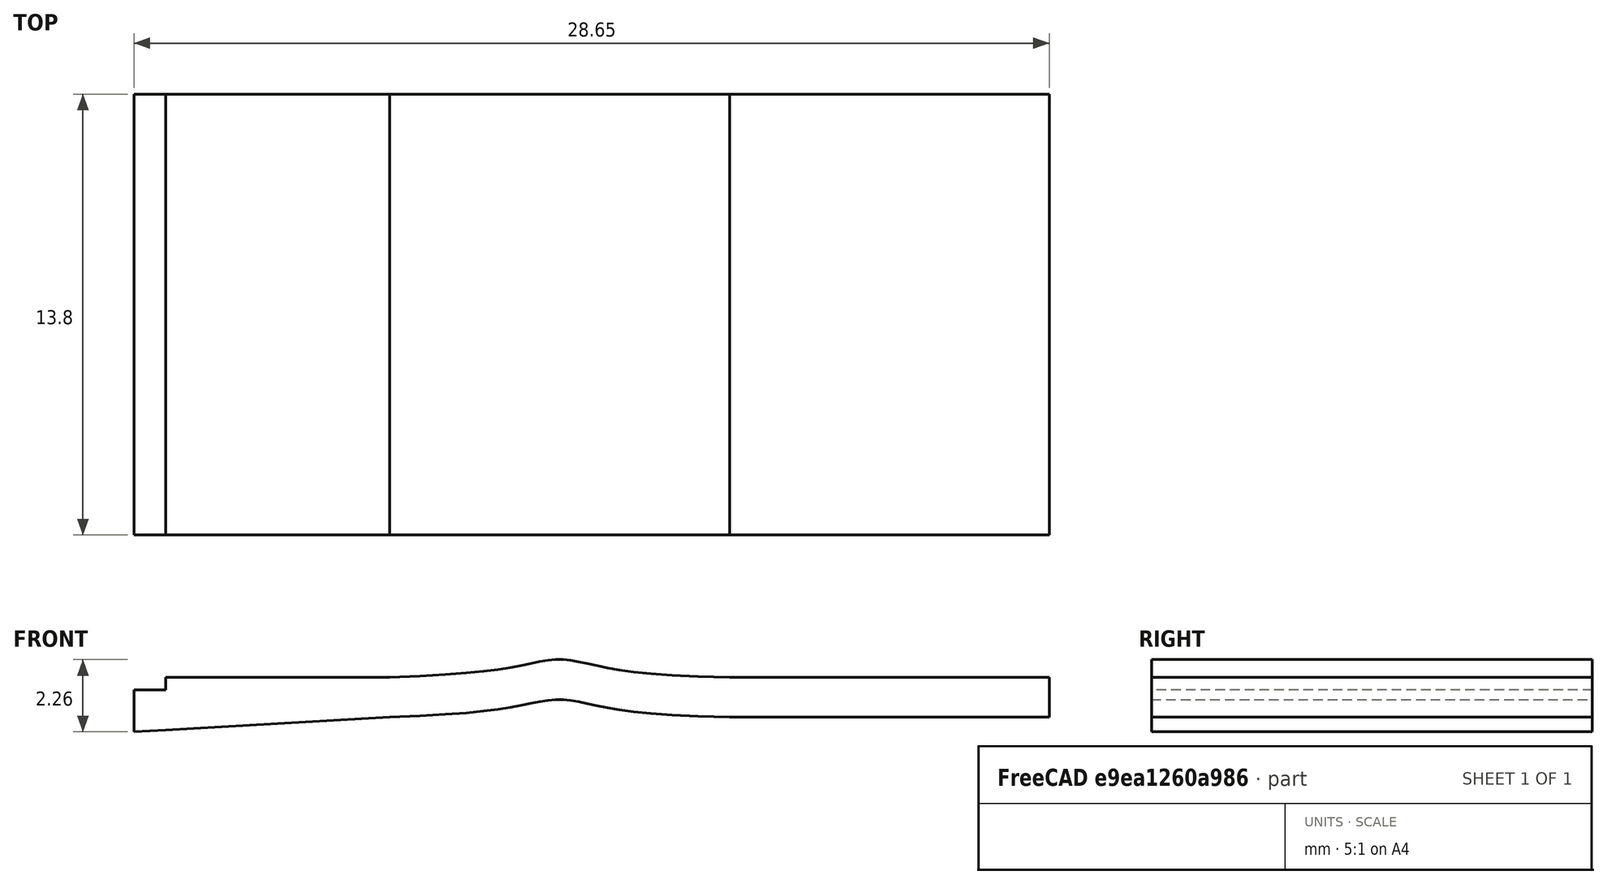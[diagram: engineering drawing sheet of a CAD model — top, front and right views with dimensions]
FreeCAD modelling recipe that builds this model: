
FCSTD DOCUMENT  (FreeCAD 0.21R33668 +26 (Git))
Label: HMV080_flex-slot-complete_channel
License: All rights reserved
LicenseURL: http://en.wikipedia.org/wiki/All_rights_reserved
objects: Sketcher::SketchObject×1, PartDesign::Pad×1, PartDesign::Body×1
note: 4 computed .brp shape members not serialized (recipe doc carries the construction recipe); baked Part::Feature solids carry a one-line shape summary decoded from their .brp

FEATURE [Sketcher::SketchObject] Sketch
  FullyConstrained = true
  MapMode = 5
  Placement = pos=(0,0,0) rot=(1,0,0;1.5708rad)
  Support = -> [XZ_Plane]
  sketch-geometry (37):
    g0: GeomPoint X=18.65 Y=0 Z=0
    g1: GeomPoint X=13.32 Y=0.7 Z=0
    g2: LineSegment StartX=18.65 StartY=0 StartZ=0 EndX=28.65 EndY=0 EndZ=0
    g3: LineSegment StartX=28.65 StartY=-1.25 StartZ=0 EndX=28.65 EndY=0 EndZ=0
    g4-g10: Circle x7 (B-spline internal-alignment scaffolding for g11; pole/knot coordinates omitted)
    g11: BSplineCurve PolesCount=7 KnotsCount=5 Degree=3 IsPeriodic=0
    g12-g16: GeomPoint x5 (B-spline internal-alignment scaffolding for g11; pole/knot coordinates omitted)
    g17: LineSegment StartX=28.65 StartY=-1.25 StartZ=0 EndX=18.65 EndY=-1.25 EndZ=0
    g18-g24: Circle x7 (B-spline internal-alignment scaffolding for g25; pole/knot coordinates omitted)
    g25: BSplineCurve PolesCount=7 KnotsCount=5 Degree=3 IsPeriodic=0
    g26-g30: GeomPoint x5 (B-spline internal-alignment scaffolding for g25; pole/knot coordinates omitted)
    g31: LineSegment StartX=1 StartY=-0.4 StartZ=0 EndX=1 EndY=0 EndZ=0
    g32: LineSegment StartX=1 StartY=0 StartZ=0 EndX=8 EndY=0 EndZ=0
    g33: LineSegment StartX=8 StartY=-1.25 StartZ=0 EndX=1 EndY=-1.65 EndZ=0
    g34: LineSegment StartX=1 StartY=-1.65 StartZ=0 EndX=0 EndY=-1.70714 EndZ=0
    g35: LineSegment StartX=0 StartY=-1.70714 StartZ=0 EndX=0 EndY=-0.4 EndZ=0
    g36: LineSegment StartX=1 StartY=-0.4 StartZ=0 EndX=0 EndY=-0.4 EndZ=0
  constraints (69):
    c: PointOnObject(g2,g-1)
    c: DistanceX(g-1,g2) = 28.65
    c: Coincident(g2,g0)
    c: Coincident(g3,g2)
    c: Vertical(g3)
    c: DistanceY(g3,g3) = 1.25
    c: Horizontal(g2)
    c: DistanceY(g-1,g1) = 0.7
    c: Weight(g4) = 1
    c: Coincident(g11,g2)
    c: Equal(g4,g5)
    c: Equal(g4,g6)
    c: Equal(g4,g7)
    c: Coincident(g7,g1)
    c: Equal(g4,g8)
    c: Equal(g4,g9)
    c: Equal(g4,g10)
    c: InternalAlignment(g4-g10 -> g11) x7
    c: InternalAlignment(g12-g16 -> g11) x5
    c: DistanceX(g9) = 9.99575
    c: DistanceY(g9) = 0.073969
    c: DistanceX(g5) = 16.551
    c: DistanceY(g5) = 0.042752
    c: DistanceX(g6) = 14.6645
    c: DistanceY(g6) = 0.25382
    c: DistanceX(g8) = 11.9505
    c: DistanceY(g8) = 0.264498
    c: Coincident(g17,g3)
    c: Horizontal(g17)
    c: Equal(g2,g17)
    c: Weight(g18) = 1
    c: Coincident(g25,g17)
    c: Equal(g18, g19-g24) x6
    c: InternalAlignment(g18-g24 -> g25) x7
    c: InternalAlignment(g26-g30 -> g25) x5
    c: DistanceY(g23,g9) = 1.25
    c: DistanceY(g22,g8) = 1.25
    c: DistanceY(g21,g1) = 1.25
    c: Vertical(g21,g1)
    c: Vertical(g9,g23)
    c: Vertical(g6,g20)
    c: DistanceY(g20,g6) = 1.25
    c: DistanceY(g19,g5) = 1.25
    c: Vertical(g5,g19)
    c: Vertical(g28,g14)
    c: PointOnObject(g11,g-1)
    c: Vertical(g11,g25)
    c: DistanceY(g25,g-1) = 1.25
    c: DistanceX(g1,g2) = 5.33
    c: DistanceX(g31) = 1
    c: DistanceY(g31) = -0.4
    c: PointOnObject(g31,g-1)
    c: Vertical(g31)
    c: Coincident(g32,g31)
    c: Coincident(g32,g11)
    c: Coincident(g33,g25)
    c: Vertical(g31,g33)
    c: DistanceY(g33,g31) = 1.25
    c: Coincident(g34,g33)
    c: PointOnObject(g34,g-2)
    c: Parallel(g34,g33)
    c: DistanceX(g2) = 18.65
    c: DistanceX(g11) = 8
    c: Coincident(g35,g34)
    c: PointOnObject(g35,g-2)
    c: Coincident(g36,g31)
    c: Coincident(g36,g35)
    c: Horizontal(g36)
    c: DistanceY(g2,g14) = 0.553053
FEATURE [PartDesign::Pad] Pad
  Direction = (0,-1,-2e-16)
  Length = 13.8
  Length2 = 10
  Placement = pos=(0,0,0) rot=(1,0,0;1.5708rad)
  Profile = -> Sketch
  ReferenceAxis = -> Sketch [N_Axis]
  Type = 0
FEATURE [PartDesign::Body] Body
  Group = -> [Sketch,Pad]
  Origin = -> Origin
  Tip = -> Pad
